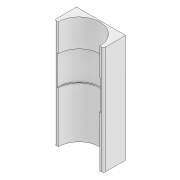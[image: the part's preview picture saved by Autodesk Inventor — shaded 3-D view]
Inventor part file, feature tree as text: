
AUTODESK INVENTOR PART (.ipt)
format: ipt  version: 2020 (Build 240168000, 168)  size: 128,000 bytes
history: native  units: mm
features: extrude x5, sketch x5, other x1, fillet x1, projected_geometry x1
ambient origin geometry x8: Origin, YZ Plane, XZ Plane, XY Plane, X Axis, Y Axis, Z Axis, Center Point
bodies: Body1 (feature_tree)
feature tree (13):
  other  "솔리드1"
  extrude  "돌출1"  Depth=50.0mm
  extrude  "돌출2"  Depth=110.0mm
  extrude  "돌출3"  Depth=41.5mm TaperAngle=0.0deg
  extrude  "돌출4"  Depth=42.4mm
  fillet  "모깎기1"  Radius=51.9mm
  extrude  "돌출5"  Depth=44.6mm
  sketch  "스케치1"
  sketch  "스케치2"
  sketch  "스케치3"
  sketch  "스케치4"
  sketch  "스케치5"
  projected_geometry  "투영된 루프1"
